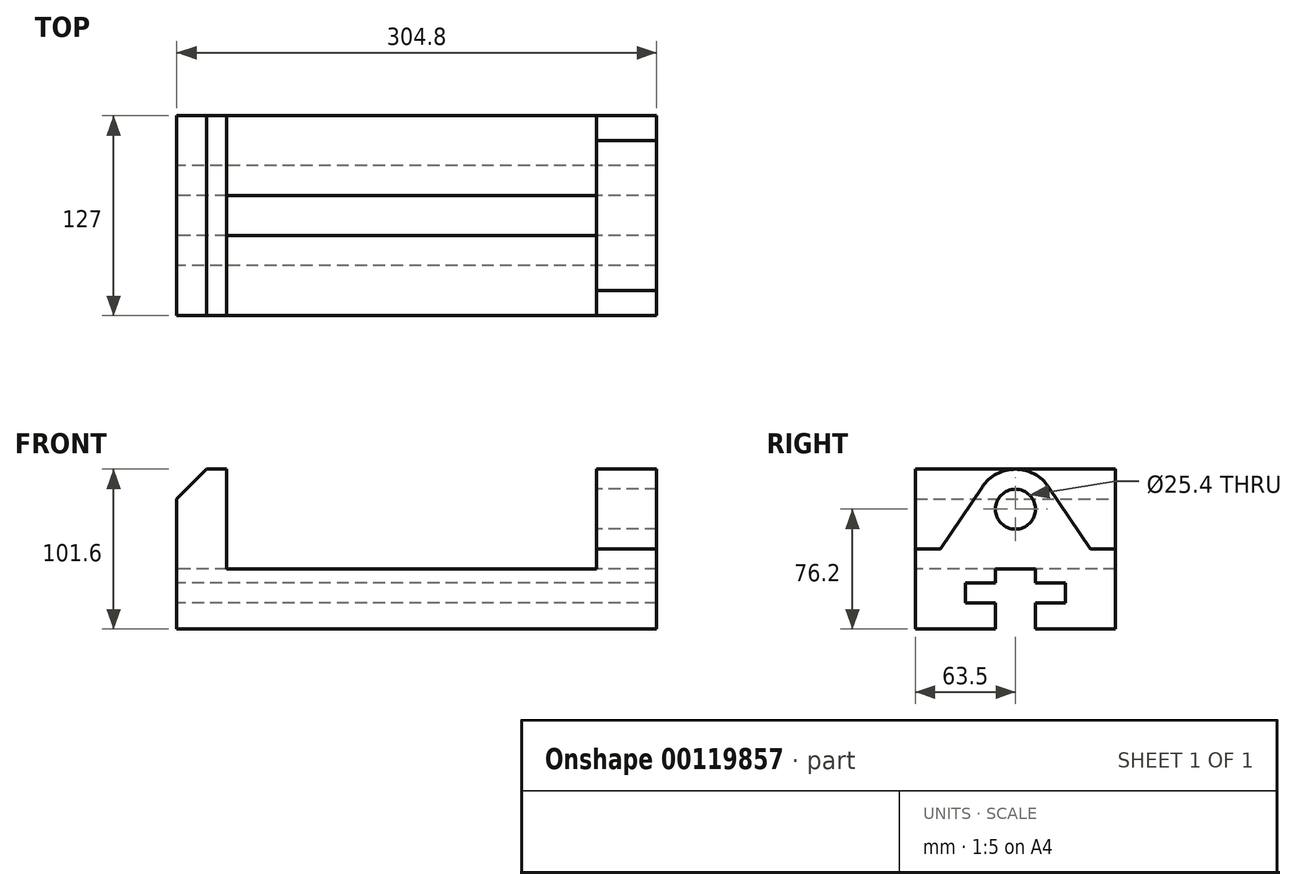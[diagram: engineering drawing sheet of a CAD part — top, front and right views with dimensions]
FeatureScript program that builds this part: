
annotation { "Feature Type Name" : "Feature", "Feature Type Description" : "" }
export const myFeature = defineFeature(function(context is Context, id is Id, definition is map)
    precondition{}
    {
        {
            var Q0;
            Q0=qCreatedBy(makeId("Right.planeOp"),FACE);
            var sketch = newSketch(context, id + "F0", { "sketchPlane" : qUnion([Q0])});
            skLineSegment(sketch, "E0.bottom", {"start": v(0, 0) * mm, "end": v(127, 0) * mm});
            skLineSegment(sketch, "E0.top", {"start": v(0, 101.6) * mm, "end": v(127, 101.6) * mm});
            skLineSegment(sketch, "E0.left", {"start": v(0, 0) * mm, "end": v(0, 101.6) * mm});
            skLineSegment(sketch, "E0.right", {"start": v(127, 0) * mm, "end": v(127, 101.6) * mm});
            skLineSegment(sketch, "E1", {"start": v(63.5, 0) * mm, "end": v(63.5, 101.6) * mm, "construction": true});
            skLineSegment(sketch, "E2", {"start": v(50.8, 0) * mm, "end": v(50.8, 16.51) * mm});
            skLineSegment(sketch, "E3", {"start": v(50.8, 16.51) * mm, "end": v(31.75, 16.51) * mm});
            skLineSegment(sketch, "E4", {"start": v(31.75, 16.51) * mm, "end": v(31.75, 29.21) * mm});
            skLineSegment(sketch, "E5", {"start": v(31.75, 29.21) * mm, "end": v(50.8, 29.21) * mm});
            skLineSegment(sketch, "E6", {"start": v(50.8, 29.21) * mm, "end": v(50.8, 38.1) * mm});
            skLineSegment(sketch, "E7", {"start": v(50.8, 38.1) * mm, "end": v(76.2, 38.1) * mm});
            skLineSegment(sketch, "E8", {"start": v(76.2, 38.1) * mm, "end": v(76.2, 29.21) * mm});
            skLineSegment(sketch, "E9", {"start": v(76.2, 29.21) * mm, "end": v(95.25, 29.21) * mm});
            skLineSegment(sketch, "E10", {"start": v(95.25, 29.21) * mm, "end": v(95.25, 16.51) * mm});
            skLineSegment(sketch, "E11", {"start": v(95.25, 16.51) * mm, "end": v(76.2, 16.51) * mm});
            skLineSegment(sketch, "E12", {"start": v(76.2, 16.51) * mm, "end": v(76.2, 0) * mm});
            skLineSegment(sketch, "E13", {"start": v(0, 50.8) * mm, "end": v(15.87, 50.8) * mm});
            skLineSegment(sketch, "E14", {"start": v(127, 50.8) * mm, "end": v(111.13, 50.8) * mm});
            skPoint(sketch, "E14.endSnap0", {"position": v(127, 50.8) * mm});
            skLineSegment(sketch, "E15", {"start": v(15.87, 50.8) * mm, "end": v(42.4, 90.35) * mm});
            skLineSegment(sketch, "E16", {"start": v(84.6, 90.35) * mm, "end": v(111.13, 50.8) * mm});
            skArc(sketch, "E17", {"start": v(84.6, 90.35) * mm, "mid": v(63.5, 101.6) * mm, "end": v(42.4, 90.35) * mm});
            skCircle(sketch, "E18", {"center": v(63.5, 76.2) * mm, "radius": 12.7 * mm});
            skSolve(sketch);
        }
        {
            var Q0;
            {var subQ4=sQuery(id+"F0.wireOp",EDGE,"E2");Q0=makeQuery(id+"F0.imprint","IMPRINT",FACE,{"disambiguationData":[TD([[makeQuery(id+"F0.imprint","IMPRINT",EDGE,{"derivedFrom":subQ4}),1.0]])]});}
            extrude(context, id + "F1", {"entities" : qUnion([Q0]), "depth" : 38.1 * mm});
        }
        {
            var Q0;
            {var subQ4=sQuery(id+"F0.wireOp",EDGE,"E14");Q0=makeQuery(id+"F0.imprint","IMPRINT",FACE,{"disambiguationData":[TD([[makeQuery(id+"F0.imprint","IMPRINT",EDGE,{"derivedFrom":subQ4}),-1.0]])]});}
            var Q1;
            {var subQ1=sQuery(id+"F0.wireOp",EDGE,"E13");Q1=makeQuery(id+"F0.imprint","IMPRINT",FACE,{"disambiguationData":[TD([[makeQuery(id+"F0.imprint","IMPRINT",EDGE,{"derivedFrom":subQ1}),1.0]])]});}
            var Q2;
            {var subQ4=sQuery(id+"F0.wireOp",EDGE,"E2");Q2=makeQuery(id+"F0.imprint","IMPRINT",FACE,{"disambiguationData":[TD([[makeQuery(id+"F0.imprint","IMPRINT",EDGE,{"derivedFrom":subQ4}),1.0]])]});}
            var Q3;
            Q3=makeQuery(id+"F0.imprint","IMPRINT",FACE,{"disambiguationData":[TD([[makeQuery(id+"F0.imprint","IMPRINT",EDGE,{"derivedFrom":sQuery(id+"F0.wireOp",EDGE,"E18")}),1.0]])]});
            extrude(context, id + "F2", {"entities" : qUnion([Q0, Q1, Q2, Q3]), "operationType" : NewBodyOperationType.ADD, "oppositeDirection" : true, "depth" : 266.7 * mm});
        }
        {
            var Q0;
            Q0=makeQuery(id+"F2.opExtrude","CAP_EDGE",EDGE,{"disambiguationData":[OSD([sQuery(id+"F0.wireOp",EDGE,"E0.top")])],"isStart":false});
            chamfer(context, id + "F3", {"entities" : qUnion([Q0]), "chamferType" : ChamferType.TWO_OFFSETS, "width1" : 19.05 * mm, "oppositeDirection" : false, "width2" : 19.05 * mm, "tangentPropagation" : true});
        }
        {
            var Q0;
            {var subQ0=sQuery(id+"F0.wireOp",EDGE,"E0.left");Q0=makeQuery(id+"F2.boolean.opBoolean","MERGE",FACE,{"derivedFrom":[makeQuery(id+"F1.opExtrude","SWEPT_FACE",FACE,{"disambiguationData":[OSD([subQ0])]}),makeQuery(id+"F2.opExtrude","SWEPT_FACE",FACE,{"disambiguationData":[OSD([subQ0])]})]});}
            var sketch = newSketch(context, id + "F4", { "sketchPlane" : qUnion([Q0])});
            skLineSegment(sketch, "E19", {"start": v(-266.7, 0) * mm, "end": v(-234.95, 0) * mm});
            skLineSegment(sketch, "E20", {"start": v(-234.95, 101.6) * mm, "end": v(-247.65, 101.6) * mm});
            skLineSegment(sketch, "E21", {"start": v(-247.65, 101.6) * mm, "end": v(-266.7, 82.55) * mm});
            skLineSegment(sketch, "E22", {"start": v(-266.7, 82.55) * mm, "end": v(-266.7, 0) * mm});
            skLineSegment(sketch, "E23", {"start": v(-234.95, 101.6) * mm, "end": v(-234.95, 0) * mm, "construction": true});
            skLineSegment(sketch, "E24", {"start": v(-234.95, 38.1) * mm, "end": v(0, 38.1) * mm});
            skLineSegment(sketch, "E25", {"start": v(0, 38.1) * mm, "end": v(0, 50.8) * mm});
            skLineSegment(sketch, "E26", {"start": v(0, 50.8) * mm, "end": v(38.1, 50.8) * mm});
            skLineSegment(sketch, "E27", {"start": v(38.1, 50.8) * mm, "end": v(38.1, 0) * mm});
            skLineSegment(sketch, "E28", {"start": v(38.1, 0) * mm, "end": v(-234.95, 0) * mm});
            skLineSegment(sketch, "E29", {"start": v(-234.95, 38.1) * mm, "end": v(-234.95, 101.6) * mm});
            skSolve(sketch);
        }
        {
            var Q0;
            Q0=makeQuery(id+"F4.imprint","IMPRINT",FACE,{"disambiguationData":[TD([[makeQuery(id+"F4.imprint","IMPRINT",EDGE,{"derivedFrom":sQuery(id+"F4.wireOp",EDGE,"E24")}),1.0]])]});
            extrude(context, id + "F5", {"entities" : qUnion([Q0]), "operationType" : NewBodyOperationType.REMOVE, "endBound" : BoundingType.THROUGH_ALL, "oppositeDirection" : true, "depth" : 25.4 * mm});
        }
    });
